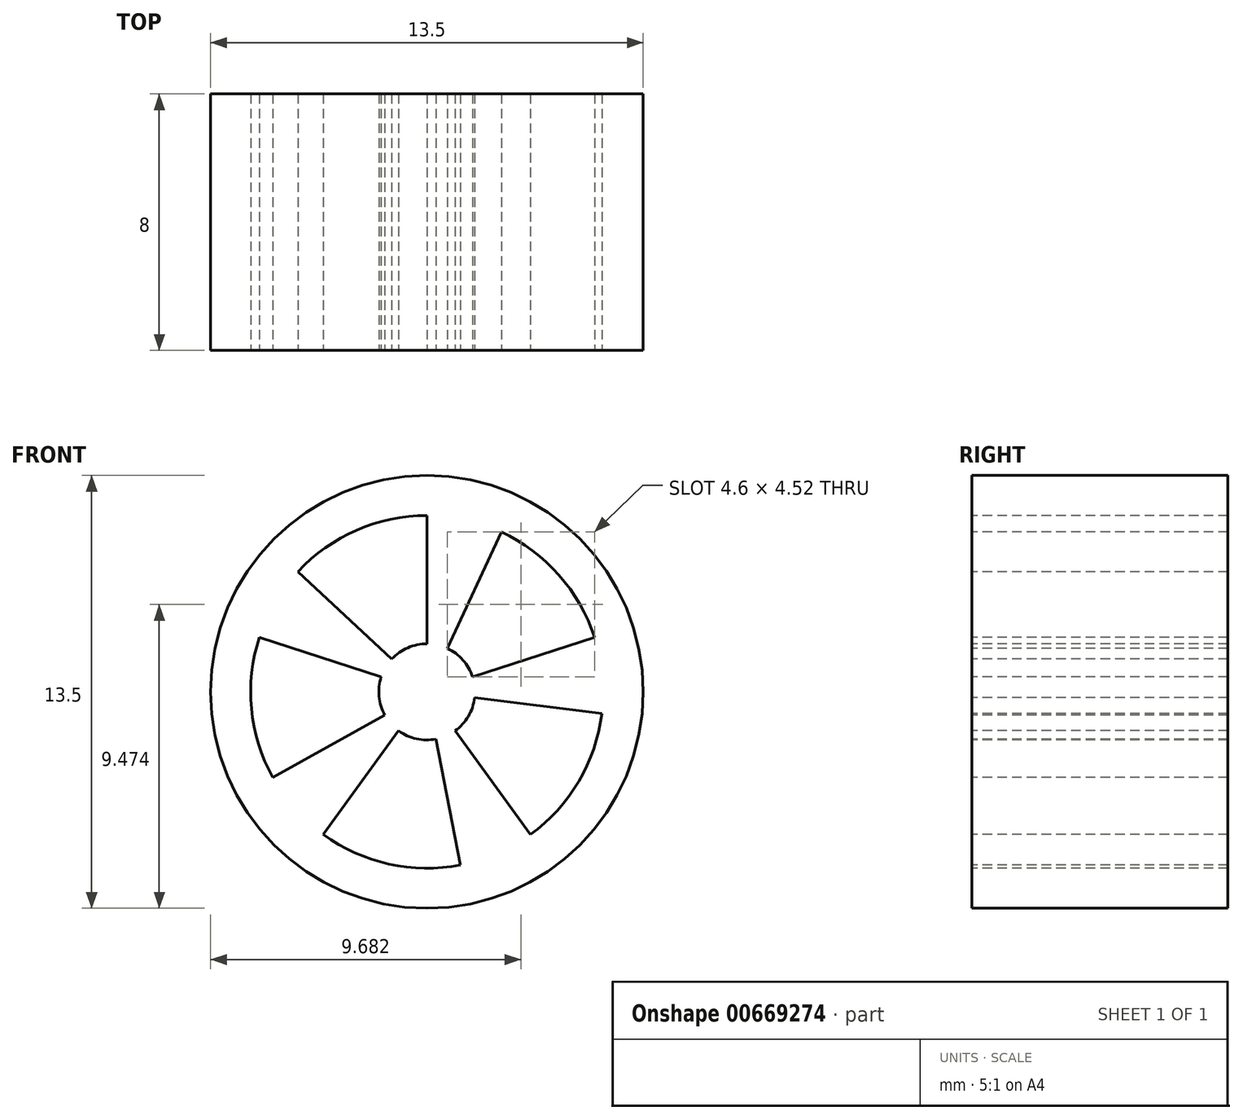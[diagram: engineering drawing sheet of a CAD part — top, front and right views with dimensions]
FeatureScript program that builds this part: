
annotation { "Feature Type Name" : "Feature", "Feature Type Description" : "" }
export const myFeature = defineFeature(function(context is Context, id is Id, definition is map)
    precondition{}
    {
        {
            var Q0;
            Q0=qCreatedBy(makeId("Front.planeOp"),FACE);
            var sketch = newSketch(context, id + "F0", { "sketchPlane" : qUnion([Q0])});
            skCircle(sketch, "E0", {"center": v(0, 0) * mm, "radius": 6.75 * mm});
            skSolve(sketch);
        }
        {
            var Q0;
            Q0=makeQuery(id+"F0.imprint","IMPRINT",FACE,{"disambiguationData":[TD([[makeQuery(id+"F0.imprint","IMPRINT",EDGE,{"derivedFrom":sQuery(id+"F0.wireOp",EDGE,"E0")}),1.0]])]});
            extrude(context, id + "F1", {"entities" : qUnion([Q0]), "depth" : 8 * mm, "offsetDistance" : 25 * mm});
        }
        {
            var Q0;
            Q0=makeQuery(id+"F1.opExtrude","CAP_FACE",FACE,{"disambiguationData":[OSD([sQuery(id+"F0.wireOp",EDGE,"E0")])],"isStart":false});
            var sketch = newSketch(context, id + "F2", { "sketchPlane" : qUnion([Q0])});
            skCircle(sketch, "E1", {"center": v(0, 0) * mm, "radius": 1.5 * mm});
            skCircle(sketch, "E2", {"center": v(0, 0) * mm, "radius": 5.5 * mm});
            skLineSegment(sketch, "E3", {"start": v(0, 1.5) * mm, "end": v(0, 5.5) * mm});
            skLineSegment(sketch, "E4", {"start": v(0.63, 1.36) * mm, "end": v(2.32, 4.98) * mm});
            skLineSegment(sketch, "E5.1.0", {"start": v(-1.43, 0.46) * mm, "end": v(-5.23, 1.7) * mm});
            skLineSegment(sketch, "E5.1.1", {"start": v(-1.1, 1.02) * mm, "end": v(-4.02, 3.75) * mm});
            skLineSegment(sketch, "E5.2.0", {"start": v(-0.88, -1.21) * mm, "end": v(-3.23, -4.45) * mm});
            skLineSegment(sketch, "E5.2.1", {"start": v(-1.31, -0.73) * mm, "end": v(-4.81, -2.67) * mm});
            skLineSegment(sketch, "E5.3.0", {"start": v(0.88, -1.21) * mm, "end": v(3.23, -4.45) * mm});
            skLineSegment(sketch, "E5.3.1", {"start": v(0.29, -1.47) * mm, "end": v(1.05, -5.4) * mm});
            skLineSegment(sketch, "E5.4.0", {"start": v(1.43, 0.46) * mm, "end": v(5.23, 1.7) * mm});
            skLineSegment(sketch, "E5.4.1", {"start": v(1.49, -0.18) * mm, "end": v(5.46, -0.67) * mm});
            skSolve(sketch);
        }
        {
            var Q0;
            {var subQ0=sQuery(id+"F2.wireOp",EDGE,"E5.1.0");Q0=makeQuery(id+"F2.imprint","IMPRINT",FACE,{"disambiguationData":[TD([[makeQuery(id+"F2.imprint","IMPRINT",EDGE,{"derivedFrom":subQ0}),1.0]])]});}
            var Q1;
            {var subQ0=sQuery(id+"F2.wireOp",EDGE,"E3");Q1=makeQuery(id+"F2.imprint","IMPRINT",FACE,{"disambiguationData":[TD([[makeQuery(id+"F2.imprint","IMPRINT",EDGE,{"derivedFrom":subQ0}),1.0]])]});}
            var Q2;
            {var subQ0=sQuery(id+"F2.wireOp",EDGE,"E4");Q2=makeQuery(id+"F2.imprint","IMPRINT",FACE,{"disambiguationData":[TD([[makeQuery(id+"F2.imprint","IMPRINT",EDGE,{"derivedFrom":subQ0}),-1.0]])]});}
            var Q3;
            {var subQ0=sQuery(id+"F2.wireOp",EDGE,"E5.3.0");Q3=makeQuery(id+"F2.imprint","IMPRINT",FACE,{"disambiguationData":[TD([[makeQuery(id+"F2.imprint","IMPRINT",EDGE,{"derivedFrom":subQ0}),1.0]])]});}
            var Q4;
            {var subQ0=sQuery(id+"F2.wireOp",EDGE,"E5.2.0");Q4=makeQuery(id+"F2.imprint","IMPRINT",FACE,{"disambiguationData":[TD([[makeQuery(id+"F2.imprint","IMPRINT",EDGE,{"derivedFrom":subQ0}),1.0]])]});}
            extrude(context, id + "F3", {"entities" : qUnion([Q0, Q1, Q2, Q3, Q4]), "operationType" : NewBodyOperationType.REMOVE, "oppositeDirection" : true, "depth" : 8 * mm, "offsetDistance" : 25 * mm});
        }
    });
